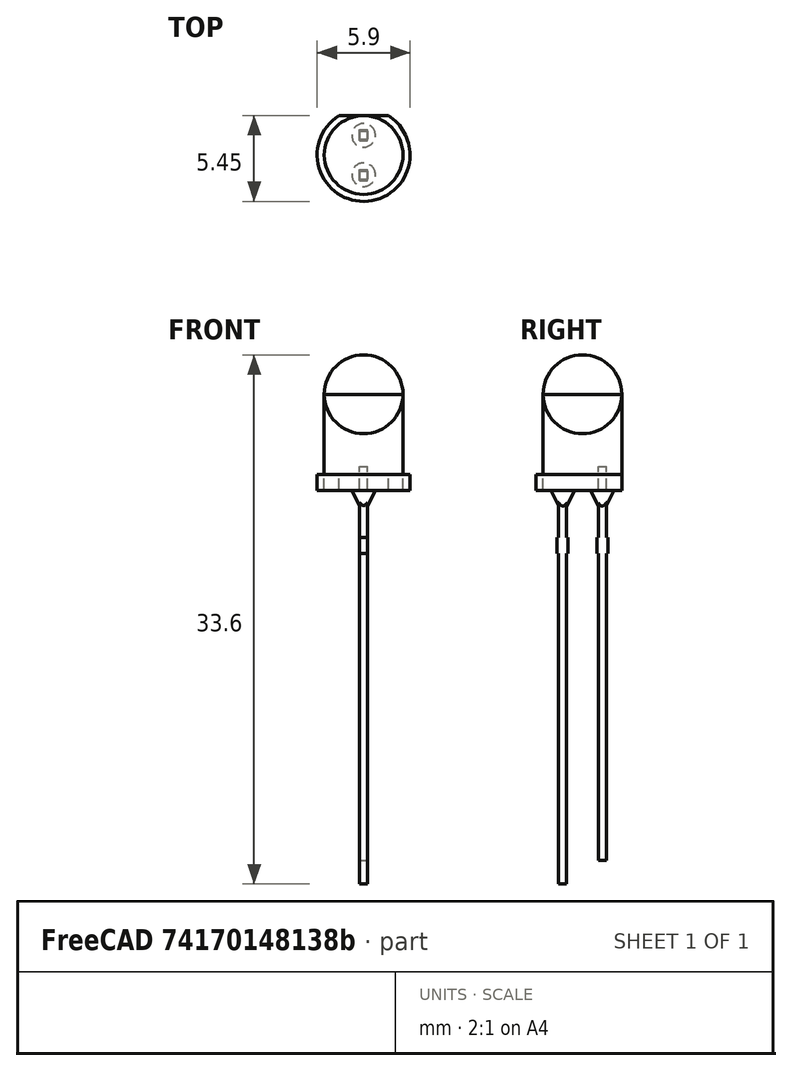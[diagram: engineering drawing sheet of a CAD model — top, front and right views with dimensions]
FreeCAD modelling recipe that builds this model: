
FCSTD DOCUMENT  (FreeCAD 0.18.3R)
Label: T1_34
License: All rights reserved
LicenseURL: http://en.wikipedia.org/wiki/All_rights_reserved
objects: Part::Box×5, Part::Cylinder×2, Part::Cone×2, Part::MultiFuse×2, Part::Sphere×1, Part::Cut×1, App::Part×1
note: 13 computed .brp shape members not serialized (recipe doc carries the construction recipe); baked Part::Feature solids carry a one-line shape summary decoded from their .brp

FEATURE [Part::Cylinder] Cylinder  label="Base cylinder"
  Angle = 360
  AttacherType = Attacher::AttachEngine3D
  Height = 1
  Radius = 2.95
FEATURE [Part::Sphere] Sphere  label="Dome"
  Angle1 = -90
  Angle2 = 90
  Angle3 = 360
  AttacherType = Attacher::AttachEngine3D
  Placement = pos=(0,0,6.1) rot=(0,0,1;0rad)
  Radius = 2.5
FEATURE [Part::Cylinder] Cylinder001  label="Encapsulant"
  Angle = 360
  AttacherType = Attacher::AttachEngine3D
  Height = 6.1
  Radius = 2.5
FEATURE [Part::Box] Box  label="Cathode flat"
  AttacherType = Attacher::AttachEngine3D
  Height = 1
  Length = 5
  Placement = pos=(-2.5,2.5,0) rot=(0,0,1;0rad)
  Width = 1
FEATURE [Part::Cut] Cut  label="Base"
  Base = -> Cylinder
  Tool = -> Box
FEATURE [Part::Cone] Cone  label="Cathode bond"
  Angle = 360
  AttacherType = Attacher::AttachEngine3D
  Height = 1
  Placement = pos=(0,1.25,-1) rot=(0,0,1;0rad)
  Radius1 = 0.25
  Radius2 = 0.75
FEATURE [Part::Box] Box001  label="Anode"
  AttacherType = Attacher::AttachEngine3D
  Height = 25
  Length = 0.5
  Placement = pos=(-0.25,-1.52,-25) rot=(0,0,1;0rad)
  Width = 0.5
FEATURE [Part::Box] Box003  label="Cathode"
  AttacherType = Attacher::AttachEngine3D
  Height = 25
  Length = 0.5
  Placement = pos=(-0.25,1.02,-23.5) rot=(0,0,1;0rad)
  Width = 0.5
FEATURE [Part::Cone] Cone001  label="Anode bond"
  Angle = 360
  AttacherType = Attacher::AttachEngine3D
  Height = 1
  Placement = pos=(0,-1.25,-1) rot=(0,0,1;0rad)
  Radius1 = 0.25
  Radius2 = 0.75
FEATURE [Part::Box] Box004  label="Anode Lead"
  AttacherType = Attacher::AttachEngine3D
  Height = 1
  Length = 0.5
  Placement = pos=(-0.25,-1.625,-4) rot=(0,0,1;0rad)
  Width = 0.7
FEATURE [Part::Box] Box005  label="Cathode Lead"
  AttacherType = Attacher::AttachEngine3D
  Height = 1
  Length = 0.5
  Placement = pos=(-0.25,0.92,-4) rot=(0,0,1;0rad)
  Width = 0.7
FEATURE [Part::MultiFuse] Fusion  label="Anode group"
  Shapes = -> [Box001,Cone001,Box004]
FEATURE [Part::MultiFuse] Fusion001  label="Cathode group"
  Shapes = -> [Box003,Cone,Box005]
FEATURE [App::Part] Part  label="T1 3/4"
  Group = -> [Cylinder,Sphere,Cylinder001,Box,Cut,Box001,Box003,Cone,Cone001,Box004,Box005,Fusion,Fusion001]
  License = CC-BY 3.0
  LicenseURL = https://creativecommons.org/licenses/by/3.0/
  Origin = -> Origin
